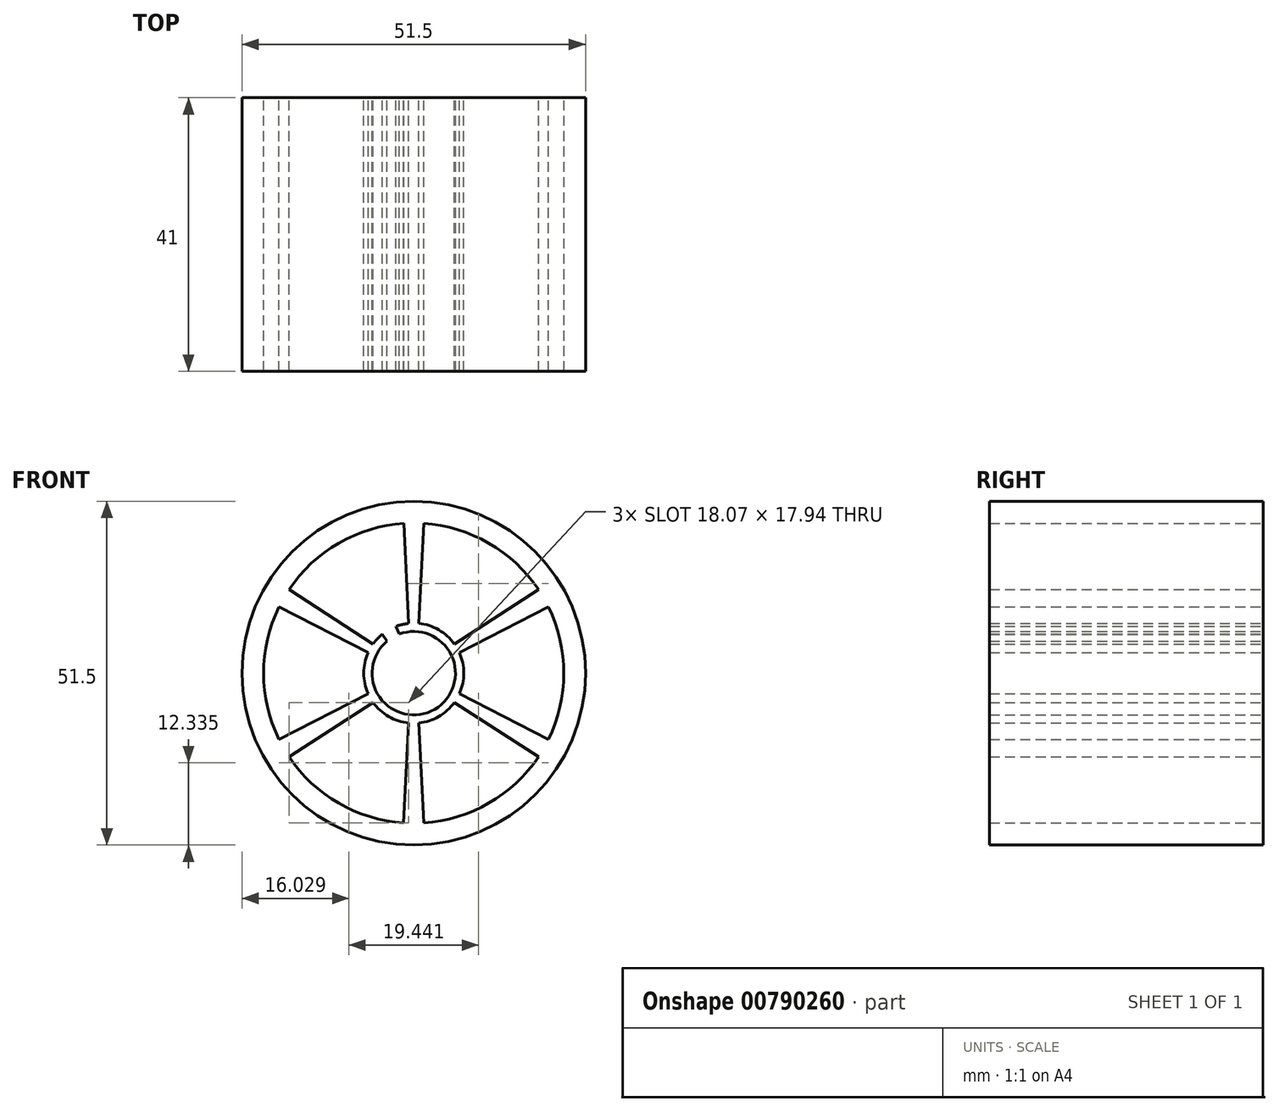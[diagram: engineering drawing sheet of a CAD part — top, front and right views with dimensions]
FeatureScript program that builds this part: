
annotation { "Feature Type Name" : "Feature", "Feature Type Description" : "" }
export const myFeature = defineFeature(function(context is Context, id is Id, definition is map)
    precondition{}
    {
        {
            var Q0;
            Q0=qCreatedBy(makeId("Front.planeOp"),FACE);
            var sketch = newSketch(context, id + "F0", { "sketchPlane" : qUnion([Q0])});
            skCircle(sketch, "E0", {"center": v(0, 0) * mm, "radius": 25.75 * mm});
            skArc(sketch, "E1", {"start": v(-4, 4.8) * mm, "mid": v(3.14, -5.4) * mm, "end": v(-2.19, 5.86) * mm});
            skLineSegment(sketch, "E2", {"start": v(1.5, 22.45) * mm, "end": v(0.75, 7.46) * mm});
            skLineSegment(sketch, "E3", {"start": v(-1.5, 22.45) * mm, "end": v(-0.75, 7.46) * mm});
            skPoint(sketch, "E4.end.orphan", {"position": v(0, 22.5) * mm});
            skPoint(sketch, "E4.start.orphan", {"position": v(0, 7.5) * mm});
            skLineSegment(sketch, "E5.anchor1", {"start": v(0, 0) * mm, "end": v(0.75, 7.46) * mm, "construction": true});
            skLineSegment(sketch, "E5.anchor2", {"start": v(0, 0) * mm, "end": v(0.75, 7.46) * mm, "construction": true});
            skLineSegment(sketch, "E6.1.0", {"start": v(-20.2, 9.93) * mm, "end": v(-6.84, 3.08) * mm});
            skLineSegment(sketch, "E6.1.1", {"start": v(-18.7, 12.52) * mm, "end": v(-6.09, 4.38) * mm});
            skLineSegment(sketch, "E6.2.0", {"start": v(-18.7, -12.52) * mm, "end": v(-6.09, -4.38) * mm});
            skLineSegment(sketch, "E6.2.1", {"start": v(-20.2, -9.93) * mm, "end": v(-6.84, -3.08) * mm});
            skLineSegment(sketch, "E6.3.0", {"start": v(1.5, -22.45) * mm, "end": v(0.75, -7.46) * mm});
            skLineSegment(sketch, "E6.3.1", {"start": v(-1.5, -22.45) * mm, "end": v(-0.75, -7.46) * mm});
            skLineSegment(sketch, "E6.4.0", {"start": v(20.2, -9.93) * mm, "end": v(6.84, -3.08) * mm});
            skLineSegment(sketch, "E6.4.1", {"start": v(18.7, -12.52) * mm, "end": v(6.09, -4.38) * mm});
            skLineSegment(sketch, "E6.5.0", {"start": v(18.7, 12.52) * mm, "end": v(6.09, 4.38) * mm});
            skLineSegment(sketch, "E6.5.1", {"start": v(20.2, 9.93) * mm, "end": v(6.84, 3.08) * mm});
            skArc(sketch, "E7.trimOffspring", {"start": v(-20.2, 9.93) * mm, "mid": v(-22.5, 0) * mm, "end": v(-20.2, -9.93) * mm});
            skArc(sketch, "E8.trimOffspring", {"start": v(-18.7, -12.52) * mm, "mid": v(-11.25, -19.49) * mm, "end": v(-1.5, -22.45) * mm});
            skArc(sketch, "E9.trimOffspring", {"start": v(20.2, -9.93) * mm, "mid": v(22.5, 0) * mm, "end": v(20.2, 9.93) * mm});
            skArc(sketch, "E10.trimOffspring", {"start": v(1.5, -22.45) * mm, "mid": v(11.25, -19.49) * mm, "end": v(18.7, -12.52) * mm});
            skArc(sketch, "E11.trimOffspring", {"start": v(-6.09, -4.38) * mm, "mid": v(-3.75, -6.5) * mm, "end": v(-0.75, -7.46) * mm});
            skArc(sketch, "E12.trimOffspring", {"start": v(0.75, -7.46) * mm, "mid": v(3.75, -6.5) * mm, "end": v(6.09, -4.38) * mm});
            skArc(sketch, "E13.trimOffspring", {"start": v(6.84, -3.08) * mm, "mid": v(7.5, 0) * mm, "end": v(6.84, 3.08) * mm});
            skArc(sketch, "E14.trimOffspring", {"start": v(6.09, 4.38) * mm, "mid": v(3.75, 6.5) * mm, "end": v(0.75, 7.46) * mm});
            skArc(sketch, "E15", {"start": v(-18.7, 12.52) * mm, "mid": v(-11.25, 19.49) * mm, "end": v(-1.5, 22.45) * mm});
            skArc(sketch, "E16", {"start": v(1.5, 22.45) * mm, "mid": v(11.25, 19.49) * mm, "end": v(18.7, 12.52) * mm});
            skArc(sketch, "E17", {"start": v(-0.75, 7.46) * mm, "mid": v(-1.74, 7.3) * mm, "end": v(-2.7, 7) * mm});
            skArc(sketch, "E18", {"start": v(-6.84, -3.08) * mm, "mid": v(-7.5, 0) * mm, "end": v(-6.84, 3.08) * mm});
            skLineSegment(sketch, "E19", {"start": v(-4.71, 5.83) * mm, "end": v(-4, 4.8) * mm});
            skLineSegment(sketch, "E20", {"start": v(-2.7, 7) * mm, "end": v(-2.19, 5.86) * mm});
            skLineSegment(sketch, "E21", {"start": v(-9.01, 6.27) * mm, "end": v(-5.04, 3.7) * mm, "construction": true});
            skLineSegment(sketch, "E22", {"start": v(-0.94, 11.28) * mm, "end": v(-0.69, 6.21) * mm, "construction": true});
            skArc(sketch, "E23.trimOffspring", {"start": v(-4.71, 5.83) * mm, "mid": v(-5.45, 5.15) * mm, "end": v(-6.09, 4.38) * mm});
            skSolve(sketch);
        }
        {
            var Q0;
            Q0=makeQuery(id+"F0.imprint","IMPRINT",FACE,{"disambiguationData":[TD([[makeQuery(id+"F0.imprint","IMPRINT",EDGE,{"derivedFrom":sQuery(id+"F0.wireOp",EDGE,"E0")}),1.0]])]});
            extrude(context, id + "F1", {"entities" : qUnion([Q0]), "depth" : 41 * mm, "offsetDistance" : 25 * mm});
        }
    });
